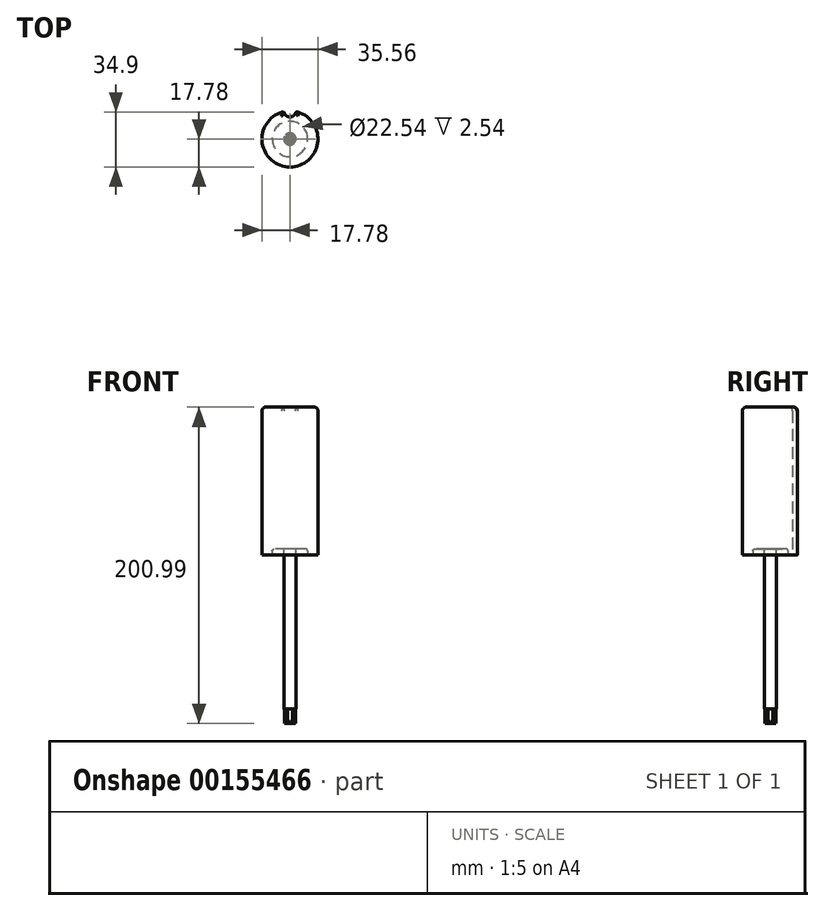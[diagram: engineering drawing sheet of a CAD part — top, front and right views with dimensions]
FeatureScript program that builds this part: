
annotation { "Feature Type Name" : "Feature", "Feature Type Description" : "" }
export const myFeature = defineFeature(function(context is Context, id is Id, definition is map)
    precondition{}
    {
        {
            var Q0;
            Q0=qCreatedBy(makeId("Top.planeOp"),FACE);
            var sketch = newSketch(context, id + "F0", { "sketchPlane" : qUnion([Q0])});
            skCircle(sketch, "E0", {"center": v(0, 0) * mm, "radius": 17.78 * mm});
            skSolve(sketch);
        }
        {
            var Q0;
            Q0=makeQuery(id+"F0.imprint","IMPRINT",FACE,{"disambiguationData":[TD([[makeQuery(id+"F0.imprint","IMPRINT",EDGE,{"derivedFrom":sQuery(id+"F0.wireOp",EDGE,"E0")}),1.0]])]});
            extrude(context, id + "F1", {"entities" : qUnion([Q0]), "depth" : 93.98 * mm});
        }
        {
            var Q0;
            Q0=qCreatedBy(makeId("Right.planeOp"),FACE);
            var sketch = newSketch(context, id + "F2", { "sketchPlane" : qUnion([Q0])});
            skLineSegment(sketch, "E1", {"start": v(0, 0) * mm, "end": v(0, -11.6) * mm});
            skLineSegment(sketch, "E2", {"start": v(0, -11.6) * mm, "end": v(8.75, -11.6) * mm});
            skLineSegment(sketch, "E3", {"start": v(8.75, -11.6) * mm, "end": v(6.7, 0) * mm});
            skLineSegment(sketch, "E4", {"start": v(6.7, 0) * mm, "end": v(0, 0) * mm});
            skSolve(sketch);
        }
        {
            var Q0;
            Q0=qCreatedBy(makeId("Top.planeOp"),FACE);
            var sketch = newSketch(context, id + "F3", { "sketchPlane" : qUnion([Q0])});
            skCircle(sketch, "E5", {"center": v(0, 17.78) * mm, "radius": 3.76 * mm});
            skSolve(sketch);
        }
        {
            var Q0;
            Q0=makeQuery(id+"F3.imprint","IMPRINT",FACE,{"disambiguationData":[TD([[makeQuery(id+"F3.imprint","IMPRINT",EDGE,{"derivedFrom":sQuery(id+"F3.wireOp",EDGE,"E5")}),1.0]])]});
            extrude(context, id + "F4", {"entities" : qUnion([Q0]), "operationType" : NewBodyOperationType.REMOVE, "depth" : 103.63 * mm});
        }
        {
            var Q0;
            Q0=makeQuery(id+"F4.boolean.opBoolean","INTERSECT",EDGE,{"disambiguationData":[OD(0.0)],"derivedFrom":[makeQuery(id+"F1.opExtrude","SWEPT_FACE",FACE,{"disambiguationData":[OSD([sQuery(id+"F0.wireOp",EDGE,"E0")])]}),makeQuery(id+"F4.opExtrude","SWEPT_FACE",FACE,{"disambiguationData":[OSD([sQuery(id+"F3.wireOp",EDGE,"E5")])]})]});
            var Q1;
            Q1=makeQuery(id+"F4.boolean.opBoolean","INTERSECT",EDGE,{"disambiguationData":[OD(1.0)],"derivedFrom":[makeQuery(id+"F1.opExtrude","SWEPT_FACE",FACE,{"disambiguationData":[OSD([sQuery(id+"F0.wireOp",EDGE,"E0")])]}),makeQuery(id+"F4.opExtrude","SWEPT_FACE",FACE,{"disambiguationData":[OSD([sQuery(id+"F3.wireOp",EDGE,"E5")])]})]});
            fillet(context, id + "F5", {"entities" : qUnion([Q0, Q1]), "radius" : 1.27 * mm, "tangentPropagation" : true, "allowEdgeOverflow" : false});
        }
        {
            var Q0;
            Q0=qCreatedBy(makeId("Top.planeOp"),FACE);
            var sketch = newSketch(context, id + "F6", { "sketchPlane" : qUnion([Q0])});
            skCircle(sketch, "E6", {"center": v(0, 0) * mm, "radius": 11.27 * mm});
            skSolve(sketch);
        }
        {
            var Q0;
            Q0=makeQuery(id+"F6.imprint","IMPRINT",FACE,{"disambiguationData":[TD([[makeQuery(id+"F6.imprint","IMPRINT",EDGE,{"derivedFrom":sQuery(id+"F6.wireOp",EDGE,"E6")}),1.0]])]});
            extrude(context, id + "F7", {"entities" : qUnion([Q0]), "operationType" : NewBodyOperationType.REMOVE, "depth" : 3.8 * mm});
        }
        {
            var Q0;
            Q0=makeQuery(id+"F7.boolean.opBoolean","COPY",EDGE,{"derivedFrom":makeQuery(id+"F7.opExtrude","CAP_EDGE",EDGE,{"disambiguationData":[OSD([sQuery(id+"F6.wireOp",EDGE,"E6")])],"isStart":true})});
            var Q1;
            Q1=makeQuery(id+"F7.boolean.opBoolean","COPY",EDGE,{"derivedFrom":makeQuery(id+"F7.opExtrude","CAP_EDGE",EDGE,{"disambiguationData":[OSD([sQuery(id+"F6.wireOp",EDGE,"E6")])],"isStart":false})});
            fillet(context, id + "F8", {"entities" : qUnion([Q0, Q1]), "radius" : 1.27 * mm, "tangentPropagation" : true, "allowEdgeOverflow" : false});
        }
        {
            var Q0;
            Q0=makeQuery(id+"F7.boolean.opBoolean","COPY",FACE,{"derivedFrom":makeQuery(id+"F7.opExtrude","CAP_FACE",FACE,{"disambiguationData":[OSD([sQuery(id+"F6.wireOp",EDGE,"E6")])],"isStart":false})});
            var sketch = newSketch(context, id + "F9", { "sketchPlane" : qUnion([Q0])});
            skCircle(sketch, "E7", {"center": v(0, 0) * mm, "radius": 3.81 * mm});
            skSolve(sketch);
        }
        {
            var Q0;
            Q0=makeQuery(id+"F9.imprint","IMPRINT",FACE,{"disambiguationData":[TD([[makeQuery(id+"F9.imprint","IMPRINT",EDGE,{"derivedFrom":sQuery(id+"F9.wireOp",EDGE,"E7")}),1.0]])]});
            extrude(context, id + "F10", {"entities" : qUnion([Q0]), "operationType" : NewBodyOperationType.ADD, "depth" : 101.6 * mm});
        }
        {
            var Q0;
            Q0=makeQuery(id+"FHcTJ38poMVbBsD_1.2.F4.boolean.opBoolean","INTERSECT",EDGE,{"derivedFrom":[makeQuery(id+"F1.opExtrude","CAP_FACE",FACE,{"disambiguationData":[OSD([sQuery(id+"F0.wireOp",EDGE,"E0")])],"isStart":false}),makeQuery(id+"FHcTJ38poMVbBsD_1.2.F4.opExtrude","SWEPT_FACE",FACE,{"disambiguationData":[OSD([sQuery(id+"F3.wireOp",EDGE,"E5")])]})]});
            var Q1;
            {var subQ0=sQuery(id+"F0.wireOp",EDGE,"E0");var subQ1=makeQuery(id+"F1.opExtrude","CAP_FACE",FACE,{"disambiguationData":[OSD([subQ0])],"isStart":false});var subQ2=sQuery(id+"F3.wireOp",EDGE,"E5");var subQ3=makeQuery(id+"F1.opExtrude","SWEPT_FACE",FACE,{"disambiguationData":[OSD([subQ0])]});Q1=makeQuery(id+"FHcTJ38poMVbBsD_1.2.F5.opFillet","BLEND_EDGE",EDGE,{"blendedFrom":[makeQuery(id+"FHcTJ38poMVbBsD_1.2.F4.boolean.opBoolean","INTERSECT",EDGE,{"disambiguationData":[OD(1.0)],"derivedFrom":[makeQuery(id+"FHcTJ38poMVbBsD_1.1.F4.boolean.opBoolean","SPLIT",FACE,{"disambiguationData":[TD([makeQuery(id+"F5.opFillet","BLEND_FACE",FACE,{"disambiguationData":[OSD([subQ0,subQ2]),TDD([makeQuery(id+"F4.boolean.opBoolean","INTERSECT",EDGE,{"disambiguationData":[OD(0.0)],"derivedFrom":[subQ3,makeQuery(id+"F4.opExtrude","SWEPT_FACE",FACE,{"disambiguationData":[OSD([subQ2])]})]})])]})])],"derivedFrom":subQ3}),makeQuery(id+"FHcTJ38poMVbBsD_1.2.F4.opExtrude","SWEPT_FACE",FACE,{"disambiguationData":[OSD([subQ2])]})]}),subQ1],"blendedInto":[subQ1]});}
            var Q2;
            {var subQ0=sQuery(id+"F0.wireOp",EDGE,"E0");var subQ1=makeQuery(id+"F1.opExtrude","SWEPT_FACE",FACE,{"disambiguationData":[OSD([subQ0])]});var subQ3=sQuery(id+"F3.wireOp",EDGE,"E5");var subQ4=makeQuery(id+"FHcTJ38poMVbBsD_1.1.F4.opExtrude","SWEPT_FACE",FACE,{"disambiguationData":[OSD([subQ3])]});Q2=makeQuery(id+"FHcTJ38poMVbBsD_1.2.F4.boolean.opBoolean","SPLIT",EDGE,{"disambiguationData":[TD([makeQuery(id+"FHcTJ38poMVbBsD_1.1.F5.opFillet","BLEND_FACE",FACE,{"disambiguationData":[OSD([subQ0,subQ3]),TDD([makeQuery(id+"FHcTJ38poMVbBsD_1.1.F4.boolean.opBoolean","INTERSECT",EDGE,{"disambiguationData":[OD(0.0)],"derivedFrom":[subQ1,subQ4]})])]})])],"derivedFrom":makeQuery(id+"FHcTJ38poMVbBsD_1.1.F4.boolean.opBoolean","SPLIT",EDGE,{"disambiguationData":[TD([makeQuery(id+"F5.opFillet","BLEND_FACE",FACE,{"disambiguationData":[OSD([subQ0,subQ3]),TDD([makeQuery(id+"F4.boolean.opBoolean","INTERSECT",EDGE,{"disambiguationData":[OD(0.0)],"derivedFrom":[subQ1,makeQuery(id+"F4.opExtrude","SWEPT_FACE",FACE,{"disambiguationData":[OSD([subQ3])]})]})])]})])],"derivedFrom":makeQuery(id+"F1.opExtrude","CAP_EDGE",EDGE,{"disambiguationData":[OSD([subQ0])],"isStart":false})})});}
            var Q3;
            Q3=makeQuery(id+"FHcTJ38poMVbBsD_1.1.F4.boolean.opBoolean","INTERSECT",EDGE,{"derivedFrom":[makeQuery(id+"F1.opExtrude","CAP_FACE",FACE,{"disambiguationData":[OSD([sQuery(id+"F0.wireOp",EDGE,"E0")])],"isStart":false}),makeQuery(id+"FHcTJ38poMVbBsD_1.1.F4.opExtrude","SWEPT_FACE",FACE,{"disambiguationData":[OSD([sQuery(id+"F3.wireOp",EDGE,"E5")])]})]});
            var Q4;
            {var subQ0=sQuery(id+"F0.wireOp",EDGE,"E0");Q4=makeQuery(id+"FHcTJ38poMVbBsD_1.1.F5.opFillet","BLEND_EDGE",EDGE,{"blendedFrom":[makeQuery(id+"FHcTJ38poMVbBsD_1.1.F4.boolean.opBoolean","INTERSECT",EDGE,{"disambiguationData":[OD(0.0)],"derivedFrom":[makeQuery(id+"F1.opExtrude","SWEPT_FACE",FACE,{"disambiguationData":[OSD([subQ0])]}),makeQuery(id+"FHcTJ38poMVbBsD_1.1.F4.opExtrude","SWEPT_FACE",FACE,{"disambiguationData":[OSD([sQuery(id+"F3.wireOp",EDGE,"E5")])]})]}),makeQuery(id+"F1.opExtrude","CAP_FACE",FACE,{"disambiguationData":[OSD([subQ0])],"isStart":false})],"blendedInto":[makeQuery(id+"F1.opExtrude","CAP_FACE",FACE,{"disambiguationData":[OSD([subQ0])],"isStart":false})]});}
            var Q5;
            {var subQ0=sQuery(id+"F0.wireOp",EDGE,"E0");Q5=makeQuery(id+"FHcTJ38poMVbBsD_1.1.F5.opFillet","BLEND_EDGE",EDGE,{"blendedFrom":[makeQuery(id+"FHcTJ38poMVbBsD_1.1.F4.boolean.opBoolean","INTERSECT",EDGE,{"disambiguationData":[OD(1.0)],"derivedFrom":[makeQuery(id+"F1.opExtrude","SWEPT_FACE",FACE,{"disambiguationData":[OSD([subQ0])]}),makeQuery(id+"FHcTJ38poMVbBsD_1.1.F4.opExtrude","SWEPT_FACE",FACE,{"disambiguationData":[OSD([sQuery(id+"F3.wireOp",EDGE,"E5")])]})]}),makeQuery(id+"F1.opExtrude","CAP_FACE",FACE,{"disambiguationData":[OSD([subQ0])],"isStart":false})],"blendedInto":[makeQuery(id+"F1.opExtrude","CAP_FACE",FACE,{"disambiguationData":[OSD([subQ0])],"isStart":false})]});}
            var Q6;
            {var subQ0=sQuery(id+"F0.wireOp",EDGE,"E0");var subQ1=makeQuery(id+"F1.opExtrude","SWEPT_FACE",FACE,{"disambiguationData":[OSD([subQ0])]});var subQ2=sQuery(id+"F3.wireOp",EDGE,"E5");Q6=makeQuery(id+"FHcTJ38poMVbBsD_1.1.F4.boolean.opBoolean","SPLIT",EDGE,{"disambiguationData":[TD([makeQuery(id+"F5.opFillet","BLEND_FACE",FACE,{"disambiguationData":[OSD([subQ0,subQ2]),TDD([makeQuery(id+"F4.boolean.opBoolean","INTERSECT",EDGE,{"disambiguationData":[OD(1.0)],"derivedFrom":[subQ1,makeQuery(id+"F4.opExtrude","SWEPT_FACE",FACE,{"disambiguationData":[OSD([subQ2])]})]})])]})])],"derivedFrom":makeQuery(id+"F1.opExtrude","CAP_EDGE",EDGE,{"disambiguationData":[OSD([subQ0])],"isStart":false})});}
            var Q7;
            {var subQ0=sQuery(id+"F0.wireOp",EDGE,"E0");Q7=makeQuery(id+"F5.opFillet","BLEND_EDGE",EDGE,{"blendedFrom":[makeQuery(id+"F4.boolean.opBoolean","INTERSECT",EDGE,{"disambiguationData":[OD(1.0)],"derivedFrom":[makeQuery(id+"F1.opExtrude","SWEPT_FACE",FACE,{"disambiguationData":[OSD([subQ0])]}),makeQuery(id+"F4.opExtrude","SWEPT_FACE",FACE,{"disambiguationData":[OSD([sQuery(id+"F3.wireOp",EDGE,"E5")])]})]}),makeQuery(id+"F1.opExtrude","CAP_FACE",FACE,{"disambiguationData":[OSD([subQ0])],"isStart":false})],"blendedInto":[makeQuery(id+"F1.opExtrude","CAP_FACE",FACE,{"disambiguationData":[OSD([subQ0])],"isStart":false})]});}
            var Q8;
            Q8=makeQuery(id+"F4.boolean.opBoolean","INTERSECT",EDGE,{"derivedFrom":[makeQuery(id+"F1.opExtrude","CAP_FACE",FACE,{"disambiguationData":[OSD([sQuery(id+"F0.wireOp",EDGE,"E0")])],"isStart":false}),makeQuery(id+"F4.opExtrude","SWEPT_FACE",FACE,{"disambiguationData":[OSD([sQuery(id+"F3.wireOp",EDGE,"E5")])]})]});
            var Q9;
            {var subQ0=sQuery(id+"F0.wireOp",EDGE,"E0");Q9=makeQuery(id+"F5.opFillet","BLEND_EDGE",EDGE,{"blendedFrom":[makeQuery(id+"F4.boolean.opBoolean","INTERSECT",EDGE,{"disambiguationData":[OD(0.0)],"derivedFrom":[makeQuery(id+"F1.opExtrude","SWEPT_FACE",FACE,{"disambiguationData":[OSD([subQ0])]}),makeQuery(id+"F4.opExtrude","SWEPT_FACE",FACE,{"disambiguationData":[OSD([sQuery(id+"F3.wireOp",EDGE,"E5")])]})]}),makeQuery(id+"F1.opExtrude","CAP_FACE",FACE,{"disambiguationData":[OSD([subQ0])],"isStart":false})],"blendedInto":[makeQuery(id+"F1.opExtrude","CAP_FACE",FACE,{"disambiguationData":[OSD([subQ0])],"isStart":false})]});}
            var Q10;
            {var subQ0=sQuery(id+"F0.wireOp",EDGE,"E0");var subQ1=makeQuery(id+"F1.opExtrude","SWEPT_FACE",FACE,{"disambiguationData":[OSD([subQ0])]});var subQ3=sQuery(id+"F3.wireOp",EDGE,"E5");var subQ4=makeQuery(id+"F5.opFillet","BLEND_FACE",FACE,{"disambiguationData":[OSD([subQ0,subQ3]),TDD([makeQuery(id+"F4.boolean.opBoolean","INTERSECT",EDGE,{"disambiguationData":[OD(0.0)],"derivedFrom":[subQ1,makeQuery(id+"F4.opExtrude","SWEPT_FACE",FACE,{"disambiguationData":[OSD([subQ3])]})]})])]});Q10=makeQuery(id+"FHcTJ38poMVbBsD_1.7.F4.boolean.opBoolean","SPLIT",EDGE,{"disambiguationData":[TD([subQ4])],"derivedFrom":makeQuery(id+"FHcTJ38poMVbBsD_1.6.F4.boolean.opBoolean","SPLIT",EDGE,{"disambiguationData":[TD([subQ4])],"derivedFrom":makeQuery(id+"FHcTJ38poMVbBsD_1.5.F4.boolean.opBoolean","SPLIT",EDGE,{"disambiguationData":[TD([subQ4])],"derivedFrom":makeQuery(id+"FHcTJ38poMVbBsD_1.4.F4.boolean.opBoolean","SPLIT",EDGE,{"disambiguationData":[TD([subQ4])],"derivedFrom":makeQuery(id+"FHcTJ38poMVbBsD_1.3.F4.boolean.opBoolean","SPLIT",EDGE,{"disambiguationData":[TD([subQ4])],"derivedFrom":makeQuery(id+"FHcTJ38poMVbBsD_1.2.F4.boolean.opBoolean","SPLIT",EDGE,{"disambiguationData":[TD([subQ4])],"derivedFrom":makeQuery(id+"FHcTJ38poMVbBsD_1.1.F4.boolean.opBoolean","SPLIT",EDGE,{"disambiguationData":[TD([subQ4])],"derivedFrom":makeQuery(id+"F1.opExtrude","CAP_EDGE",EDGE,{"disambiguationData":[OSD([subQ0])],"isStart":false})})})})})})})});}
            var Q11;
            {var subQ0=sQuery(id+"F0.wireOp",EDGE,"E0");var subQ1=makeQuery(id+"F1.opExtrude","CAP_FACE",FACE,{"disambiguationData":[OSD([subQ0])],"isStart":false});var subQ2=sQuery(id+"F3.wireOp",EDGE,"E5");var subQ4=makeQuery(id+"F1.opExtrude","SWEPT_FACE",FACE,{"disambiguationData":[OSD([subQ0])]});var subQ5=makeQuery(id+"F5.opFillet","BLEND_FACE",FACE,{"disambiguationData":[OSD([subQ0,subQ2]),TDD([makeQuery(id+"F4.boolean.opBoolean","INTERSECT",EDGE,{"disambiguationData":[OD(0.0)],"derivedFrom":[subQ4,makeQuery(id+"F4.opExtrude","SWEPT_FACE",FACE,{"disambiguationData":[OSD([subQ2])]})]})])]});Q11=makeQuery(id+"FHcTJ38poMVbBsD_1.7.F5.opFillet","BLEND_EDGE",EDGE,{"blendedFrom":[makeQuery(id+"FHcTJ38poMVbBsD_1.7.F4.boolean.opBoolean","INTERSECT",EDGE,{"disambiguationData":[OD(0.0)],"derivedFrom":[makeQuery(id+"FHcTJ38poMVbBsD_1.6.F4.boolean.opBoolean","SPLIT",FACE,{"disambiguationData":[TD([subQ5])],"derivedFrom":makeQuery(id+"FHcTJ38poMVbBsD_1.5.F4.boolean.opBoolean","SPLIT",FACE,{"disambiguationData":[TD([subQ5])],"derivedFrom":makeQuery(id+"FHcTJ38poMVbBsD_1.4.F4.boolean.opBoolean","SPLIT",FACE,{"disambiguationData":[TD([subQ5])],"derivedFrom":makeQuery(id+"FHcTJ38poMVbBsD_1.3.F4.boolean.opBoolean","SPLIT",FACE,{"disambiguationData":[TD([subQ5])],"derivedFrom":makeQuery(id+"FHcTJ38poMVbBsD_1.2.F4.boolean.opBoolean","SPLIT",FACE,{"disambiguationData":[TD([subQ5])],"derivedFrom":makeQuery(id+"FHcTJ38poMVbBsD_1.1.F4.boolean.opBoolean","SPLIT",FACE,{"disambiguationData":[TD([subQ5])],"derivedFrom":subQ4})})})})})}),makeQuery(id+"FHcTJ38poMVbBsD_1.7.F4.opExtrude","SWEPT_FACE",FACE,{"disambiguationData":[OSD([subQ2])]})]}),subQ1],"blendedInto":[subQ1]});}
            var Q12;
            Q12=makeQuery(id+"FHcTJ38poMVbBsD_1.7.F4.boolean.opBoolean","INTERSECT",EDGE,{"derivedFrom":[makeQuery(id+"F1.opExtrude","CAP_FACE",FACE,{"disambiguationData":[OSD([sQuery(id+"F0.wireOp",EDGE,"E0")])],"isStart":false}),makeQuery(id+"FHcTJ38poMVbBsD_1.7.F4.opExtrude","SWEPT_FACE",FACE,{"disambiguationData":[OSD([sQuery(id+"F3.wireOp",EDGE,"E5")])]})]});
            var Q13;
            {var subQ0=sQuery(id+"F0.wireOp",EDGE,"E0");var subQ1=makeQuery(id+"F1.opExtrude","CAP_FACE",FACE,{"disambiguationData":[OSD([subQ0])],"isStart":false});var subQ2=sQuery(id+"F3.wireOp",EDGE,"E5");var subQ4=makeQuery(id+"F1.opExtrude","SWEPT_FACE",FACE,{"disambiguationData":[OSD([subQ0])]});var subQ5=makeQuery(id+"F5.opFillet","BLEND_FACE",FACE,{"disambiguationData":[OSD([subQ0,subQ2]),TDD([makeQuery(id+"F4.boolean.opBoolean","INTERSECT",EDGE,{"disambiguationData":[OD(0.0)],"derivedFrom":[subQ4,makeQuery(id+"F4.opExtrude","SWEPT_FACE",FACE,{"disambiguationData":[OSD([subQ2])]})]})])]});Q13=makeQuery(id+"FHcTJ38poMVbBsD_1.7.F5.opFillet","BLEND_EDGE",EDGE,{"blendedFrom":[makeQuery(id+"FHcTJ38poMVbBsD_1.7.F4.boolean.opBoolean","INTERSECT",EDGE,{"disambiguationData":[OD(1.0)],"derivedFrom":[makeQuery(id+"FHcTJ38poMVbBsD_1.6.F4.boolean.opBoolean","SPLIT",FACE,{"disambiguationData":[TD([subQ5])],"derivedFrom":makeQuery(id+"FHcTJ38poMVbBsD_1.5.F4.boolean.opBoolean","SPLIT",FACE,{"disambiguationData":[TD([subQ5])],"derivedFrom":makeQuery(id+"FHcTJ38poMVbBsD_1.4.F4.boolean.opBoolean","SPLIT",FACE,{"disambiguationData":[TD([subQ5])],"derivedFrom":makeQuery(id+"FHcTJ38poMVbBsD_1.3.F4.boolean.opBoolean","SPLIT",FACE,{"disambiguationData":[TD([subQ5])],"derivedFrom":makeQuery(id+"FHcTJ38poMVbBsD_1.2.F4.boolean.opBoolean","SPLIT",FACE,{"disambiguationData":[TD([subQ5])],"derivedFrom":makeQuery(id+"FHcTJ38poMVbBsD_1.1.F4.boolean.opBoolean","SPLIT",FACE,{"disambiguationData":[TD([subQ5])],"derivedFrom":subQ4})})})})})}),makeQuery(id+"FHcTJ38poMVbBsD_1.7.F4.opExtrude","SWEPT_FACE",FACE,{"disambiguationData":[OSD([subQ2])]})]}),subQ1],"blendedInto":[subQ1]});}
            var Q14;
            {var subQ0=sQuery(id+"F0.wireOp",EDGE,"E0");var subQ1=makeQuery(id+"F1.opExtrude","SWEPT_FACE",FACE,{"disambiguationData":[OSD([subQ0])]});var subQ2=sQuery(id+"F3.wireOp",EDGE,"E5");var subQ3=makeQuery(id+"FHcTJ38poMVbBsD_1.6.F4.opExtrude","SWEPT_FACE",FACE,{"disambiguationData":[OSD([subQ2])]});var subQ7=makeQuery(id+"F5.opFillet","BLEND_FACE",FACE,{"disambiguationData":[OSD([subQ0,subQ2]),TDD([makeQuery(id+"F4.boolean.opBoolean","INTERSECT",EDGE,{"disambiguationData":[OD(0.0)],"derivedFrom":[subQ1,makeQuery(id+"F4.opExtrude","SWEPT_FACE",FACE,{"disambiguationData":[OSD([subQ2])]})]})])]});Q14=makeQuery(id+"FHcTJ38poMVbBsD_1.7.F4.boolean.opBoolean","SPLIT",EDGE,{"disambiguationData":[TD([makeQuery(id+"FHcTJ38poMVbBsD_1.6.F5.opFillet","BLEND_FACE",FACE,{"disambiguationData":[OSD([subQ0,subQ2]),TDD([makeQuery(id+"FHcTJ38poMVbBsD_1.6.F4.boolean.opBoolean","INTERSECT",EDGE,{"disambiguationData":[OD(0.0)],"derivedFrom":[makeQuery(id+"FHcTJ38poMVbBsD_1.5.F4.boolean.opBoolean","SPLIT",FACE,{"disambiguationData":[TD([subQ7])],"derivedFrom":makeQuery(id+"FHcTJ38poMVbBsD_1.4.F4.boolean.opBoolean","SPLIT",FACE,{"disambiguationData":[TD([subQ7])],"derivedFrom":makeQuery(id+"FHcTJ38poMVbBsD_1.3.F4.boolean.opBoolean","SPLIT",FACE,{"disambiguationData":[TD([subQ7])],"derivedFrom":makeQuery(id+"FHcTJ38poMVbBsD_1.2.F4.boolean.opBoolean","SPLIT",FACE,{"disambiguationData":[TD([subQ7])],"derivedFrom":makeQuery(id+"FHcTJ38poMVbBsD_1.1.F4.boolean.opBoolean","SPLIT",FACE,{"disambiguationData":[TD([subQ7])],"derivedFrom":subQ1})})})})}),subQ3]})])]})])],"derivedFrom":makeQuery(id+"FHcTJ38poMVbBsD_1.6.F4.boolean.opBoolean","SPLIT",EDGE,{"disambiguationData":[TD([subQ7])],"derivedFrom":makeQuery(id+"FHcTJ38poMVbBsD_1.5.F4.boolean.opBoolean","SPLIT",EDGE,{"disambiguationData":[TD([subQ7])],"derivedFrom":makeQuery(id+"FHcTJ38poMVbBsD_1.4.F4.boolean.opBoolean","SPLIT",EDGE,{"disambiguationData":[TD([subQ7])],"derivedFrom":makeQuery(id+"FHcTJ38poMVbBsD_1.3.F4.boolean.opBoolean","SPLIT",EDGE,{"disambiguationData":[TD([subQ7])],"derivedFrom":makeQuery(id+"FHcTJ38poMVbBsD_1.2.F4.boolean.opBoolean","SPLIT",EDGE,{"disambiguationData":[TD([subQ7])],"derivedFrom":makeQuery(id+"FHcTJ38poMVbBsD_1.1.F4.boolean.opBoolean","SPLIT",EDGE,{"disambiguationData":[TD([subQ7])],"derivedFrom":makeQuery(id+"F1.opExtrude","CAP_EDGE",EDGE,{"disambiguationData":[OSD([subQ0])],"isStart":false})})})})})})})});}
            var Q15;
            {var subQ0=sQuery(id+"F0.wireOp",EDGE,"E0");var subQ1=makeQuery(id+"F1.opExtrude","CAP_FACE",FACE,{"disambiguationData":[OSD([subQ0])],"isStart":false});var subQ2=sQuery(id+"F3.wireOp",EDGE,"E5");var subQ4=makeQuery(id+"F1.opExtrude","SWEPT_FACE",FACE,{"disambiguationData":[OSD([subQ0])]});var subQ5=makeQuery(id+"F5.opFillet","BLEND_FACE",FACE,{"disambiguationData":[OSD([subQ0,subQ2]),TDD([makeQuery(id+"F4.boolean.opBoolean","INTERSECT",EDGE,{"disambiguationData":[OD(0.0)],"derivedFrom":[subQ4,makeQuery(id+"F4.opExtrude","SWEPT_FACE",FACE,{"disambiguationData":[OSD([subQ2])]})]})])]});Q15=makeQuery(id+"FHcTJ38poMVbBsD_1.6.F5.opFillet","BLEND_EDGE",EDGE,{"blendedFrom":[makeQuery(id+"FHcTJ38poMVbBsD_1.6.F4.boolean.opBoolean","INTERSECT",EDGE,{"disambiguationData":[OD(0.0)],"derivedFrom":[makeQuery(id+"FHcTJ38poMVbBsD_1.5.F4.boolean.opBoolean","SPLIT",FACE,{"disambiguationData":[TD([subQ5])],"derivedFrom":makeQuery(id+"FHcTJ38poMVbBsD_1.4.F4.boolean.opBoolean","SPLIT",FACE,{"disambiguationData":[TD([subQ5])],"derivedFrom":makeQuery(id+"FHcTJ38poMVbBsD_1.3.F4.boolean.opBoolean","SPLIT",FACE,{"disambiguationData":[TD([subQ5])],"derivedFrom":makeQuery(id+"FHcTJ38poMVbBsD_1.2.F4.boolean.opBoolean","SPLIT",FACE,{"disambiguationData":[TD([subQ5])],"derivedFrom":makeQuery(id+"FHcTJ38poMVbBsD_1.1.F4.boolean.opBoolean","SPLIT",FACE,{"disambiguationData":[TD([subQ5])],"derivedFrom":subQ4})})})})}),makeQuery(id+"FHcTJ38poMVbBsD_1.6.F4.opExtrude","SWEPT_FACE",FACE,{"disambiguationData":[OSD([subQ2])]})]}),subQ1],"blendedInto":[subQ1]});}
            var Q16;
            Q16=makeQuery(id+"FHcTJ38poMVbBsD_1.6.F4.boolean.opBoolean","INTERSECT",EDGE,{"derivedFrom":[makeQuery(id+"F1.opExtrude","CAP_FACE",FACE,{"disambiguationData":[OSD([sQuery(id+"F0.wireOp",EDGE,"E0")])],"isStart":false}),makeQuery(id+"FHcTJ38poMVbBsD_1.6.F4.opExtrude","SWEPT_FACE",FACE,{"disambiguationData":[OSD([sQuery(id+"F3.wireOp",EDGE,"E5")])]})]});
            var Q17;
            {var subQ0=sQuery(id+"F0.wireOp",EDGE,"E0");var subQ1=makeQuery(id+"F1.opExtrude","CAP_FACE",FACE,{"disambiguationData":[OSD([subQ0])],"isStart":false});var subQ2=sQuery(id+"F3.wireOp",EDGE,"E5");var subQ4=makeQuery(id+"F1.opExtrude","SWEPT_FACE",FACE,{"disambiguationData":[OSD([subQ0])]});var subQ5=makeQuery(id+"F5.opFillet","BLEND_FACE",FACE,{"disambiguationData":[OSD([subQ0,subQ2]),TDD([makeQuery(id+"F4.boolean.opBoolean","INTERSECT",EDGE,{"disambiguationData":[OD(0.0)],"derivedFrom":[subQ4,makeQuery(id+"F4.opExtrude","SWEPT_FACE",FACE,{"disambiguationData":[OSD([subQ2])]})]})])]});Q17=makeQuery(id+"FHcTJ38poMVbBsD_1.6.F5.opFillet","BLEND_EDGE",EDGE,{"blendedFrom":[makeQuery(id+"FHcTJ38poMVbBsD_1.6.F4.boolean.opBoolean","INTERSECT",EDGE,{"disambiguationData":[OD(1.0)],"derivedFrom":[makeQuery(id+"FHcTJ38poMVbBsD_1.5.F4.boolean.opBoolean","SPLIT",FACE,{"disambiguationData":[TD([subQ5])],"derivedFrom":makeQuery(id+"FHcTJ38poMVbBsD_1.4.F4.boolean.opBoolean","SPLIT",FACE,{"disambiguationData":[TD([subQ5])],"derivedFrom":makeQuery(id+"FHcTJ38poMVbBsD_1.3.F4.boolean.opBoolean","SPLIT",FACE,{"disambiguationData":[TD([subQ5])],"derivedFrom":makeQuery(id+"FHcTJ38poMVbBsD_1.2.F4.boolean.opBoolean","SPLIT",FACE,{"disambiguationData":[TD([subQ5])],"derivedFrom":makeQuery(id+"FHcTJ38poMVbBsD_1.1.F4.boolean.opBoolean","SPLIT",FACE,{"disambiguationData":[TD([subQ5])],"derivedFrom":subQ4})})})})}),makeQuery(id+"FHcTJ38poMVbBsD_1.6.F4.opExtrude","SWEPT_FACE",FACE,{"disambiguationData":[OSD([subQ2])]})]}),subQ1],"blendedInto":[subQ1]});}
            var Q18;
            {var subQ0=sQuery(id+"F0.wireOp",EDGE,"E0");var subQ1=makeQuery(id+"F1.opExtrude","SWEPT_FACE",FACE,{"disambiguationData":[OSD([subQ0])]});var subQ2=sQuery(id+"F3.wireOp",EDGE,"E5");var subQ4=makeQuery(id+"FHcTJ38poMVbBsD_1.5.F4.opExtrude","SWEPT_FACE",FACE,{"disambiguationData":[OSD([subQ2])]});var subQ7=makeQuery(id+"F5.opFillet","BLEND_FACE",FACE,{"disambiguationData":[OSD([subQ0,subQ2]),TDD([makeQuery(id+"F4.boolean.opBoolean","INTERSECT",EDGE,{"disambiguationData":[OD(0.0)],"derivedFrom":[subQ1,makeQuery(id+"F4.opExtrude","SWEPT_FACE",FACE,{"disambiguationData":[OSD([subQ2])]})]})])]});Q18=makeQuery(id+"FHcTJ38poMVbBsD_1.6.F4.boolean.opBoolean","SPLIT",EDGE,{"disambiguationData":[TD([makeQuery(id+"FHcTJ38poMVbBsD_1.5.F5.opFillet","BLEND_FACE",FACE,{"disambiguationData":[OSD([subQ0,subQ2]),TDD([makeQuery(id+"FHcTJ38poMVbBsD_1.5.F4.boolean.opBoolean","INTERSECT",EDGE,{"disambiguationData":[OD(0.0)],"derivedFrom":[makeQuery(id+"FHcTJ38poMVbBsD_1.4.F4.boolean.opBoolean","SPLIT",FACE,{"disambiguationData":[TD([subQ7])],"derivedFrom":makeQuery(id+"FHcTJ38poMVbBsD_1.3.F4.boolean.opBoolean","SPLIT",FACE,{"disambiguationData":[TD([subQ7])],"derivedFrom":makeQuery(id+"FHcTJ38poMVbBsD_1.2.F4.boolean.opBoolean","SPLIT",FACE,{"disambiguationData":[TD([subQ7])],"derivedFrom":makeQuery(id+"FHcTJ38poMVbBsD_1.1.F4.boolean.opBoolean","SPLIT",FACE,{"disambiguationData":[TD([subQ7])],"derivedFrom":subQ1})})})}),subQ4]})])]})])],"derivedFrom":makeQuery(id+"FHcTJ38poMVbBsD_1.5.F4.boolean.opBoolean","SPLIT",EDGE,{"disambiguationData":[TD([subQ7])],"derivedFrom":makeQuery(id+"FHcTJ38poMVbBsD_1.4.F4.boolean.opBoolean","SPLIT",EDGE,{"disambiguationData":[TD([subQ7])],"derivedFrom":makeQuery(id+"FHcTJ38poMVbBsD_1.3.F4.boolean.opBoolean","SPLIT",EDGE,{"disambiguationData":[TD([subQ7])],"derivedFrom":makeQuery(id+"FHcTJ38poMVbBsD_1.2.F4.boolean.opBoolean","SPLIT",EDGE,{"disambiguationData":[TD([subQ7])],"derivedFrom":makeQuery(id+"FHcTJ38poMVbBsD_1.1.F4.boolean.opBoolean","SPLIT",EDGE,{"disambiguationData":[TD([subQ7])],"derivedFrom":makeQuery(id+"F1.opExtrude","CAP_EDGE",EDGE,{"disambiguationData":[OSD([subQ0])],"isStart":false})})})})})})});}
            var Q19;
            {var subQ0=sQuery(id+"F0.wireOp",EDGE,"E0");var subQ1=makeQuery(id+"F1.opExtrude","CAP_FACE",FACE,{"disambiguationData":[OSD([subQ0])],"isStart":false});var subQ2=sQuery(id+"F3.wireOp",EDGE,"E5");var subQ4=makeQuery(id+"F1.opExtrude","SWEPT_FACE",FACE,{"disambiguationData":[OSD([subQ0])]});var subQ5=makeQuery(id+"F5.opFillet","BLEND_FACE",FACE,{"disambiguationData":[OSD([subQ0,subQ2]),TDD([makeQuery(id+"F4.boolean.opBoolean","INTERSECT",EDGE,{"disambiguationData":[OD(0.0)],"derivedFrom":[subQ4,makeQuery(id+"F4.opExtrude","SWEPT_FACE",FACE,{"disambiguationData":[OSD([subQ2])]})]})])]});Q19=makeQuery(id+"FHcTJ38poMVbBsD_1.5.F5.opFillet","BLEND_EDGE",EDGE,{"blendedFrom":[makeQuery(id+"FHcTJ38poMVbBsD_1.5.F4.boolean.opBoolean","INTERSECT",EDGE,{"disambiguationData":[OD(0.0)],"derivedFrom":[makeQuery(id+"FHcTJ38poMVbBsD_1.4.F4.boolean.opBoolean","SPLIT",FACE,{"disambiguationData":[TD([subQ5])],"derivedFrom":makeQuery(id+"FHcTJ38poMVbBsD_1.3.F4.boolean.opBoolean","SPLIT",FACE,{"disambiguationData":[TD([subQ5])],"derivedFrom":makeQuery(id+"FHcTJ38poMVbBsD_1.2.F4.boolean.opBoolean","SPLIT",FACE,{"disambiguationData":[TD([subQ5])],"derivedFrom":makeQuery(id+"FHcTJ38poMVbBsD_1.1.F4.boolean.opBoolean","SPLIT",FACE,{"disambiguationData":[TD([subQ5])],"derivedFrom":subQ4})})})}),makeQuery(id+"FHcTJ38poMVbBsD_1.5.F4.opExtrude","SWEPT_FACE",FACE,{"disambiguationData":[OSD([subQ2])]})]}),subQ1],"blendedInto":[subQ1]});}
            var Q20;
            Q20=makeQuery(id+"FHcTJ38poMVbBsD_1.5.F4.boolean.opBoolean","INTERSECT",EDGE,{"derivedFrom":[makeQuery(id+"F1.opExtrude","CAP_FACE",FACE,{"disambiguationData":[OSD([sQuery(id+"F0.wireOp",EDGE,"E0")])],"isStart":false}),makeQuery(id+"FHcTJ38poMVbBsD_1.5.F4.opExtrude","SWEPT_FACE",FACE,{"disambiguationData":[OSD([sQuery(id+"F3.wireOp",EDGE,"E5")])]})]});
            var Q21;
            {var subQ0=sQuery(id+"F0.wireOp",EDGE,"E0");var subQ1=makeQuery(id+"F1.opExtrude","CAP_FACE",FACE,{"disambiguationData":[OSD([subQ0])],"isStart":false});var subQ2=sQuery(id+"F3.wireOp",EDGE,"E5");var subQ4=makeQuery(id+"F1.opExtrude","SWEPT_FACE",FACE,{"disambiguationData":[OSD([subQ0])]});var subQ5=makeQuery(id+"F5.opFillet","BLEND_FACE",FACE,{"disambiguationData":[OSD([subQ0,subQ2]),TDD([makeQuery(id+"F4.boolean.opBoolean","INTERSECT",EDGE,{"disambiguationData":[OD(0.0)],"derivedFrom":[subQ4,makeQuery(id+"F4.opExtrude","SWEPT_FACE",FACE,{"disambiguationData":[OSD([subQ2])]})]})])]});Q21=makeQuery(id+"FHcTJ38poMVbBsD_1.5.F5.opFillet","BLEND_EDGE",EDGE,{"blendedFrom":[makeQuery(id+"FHcTJ38poMVbBsD_1.5.F4.boolean.opBoolean","INTERSECT",EDGE,{"disambiguationData":[OD(1.0)],"derivedFrom":[makeQuery(id+"FHcTJ38poMVbBsD_1.4.F4.boolean.opBoolean","SPLIT",FACE,{"disambiguationData":[TD([subQ5])],"derivedFrom":makeQuery(id+"FHcTJ38poMVbBsD_1.3.F4.boolean.opBoolean","SPLIT",FACE,{"disambiguationData":[TD([subQ5])],"derivedFrom":makeQuery(id+"FHcTJ38poMVbBsD_1.2.F4.boolean.opBoolean","SPLIT",FACE,{"disambiguationData":[TD([subQ5])],"derivedFrom":makeQuery(id+"FHcTJ38poMVbBsD_1.1.F4.boolean.opBoolean","SPLIT",FACE,{"disambiguationData":[TD([subQ5])],"derivedFrom":subQ4})})})}),makeQuery(id+"FHcTJ38poMVbBsD_1.5.F4.opExtrude","SWEPT_FACE",FACE,{"disambiguationData":[OSD([subQ2])]})]}),subQ1],"blendedInto":[subQ1]});}
            var Q22;
            {var subQ0=sQuery(id+"F0.wireOp",EDGE,"E0");var subQ1=makeQuery(id+"F1.opExtrude","SWEPT_FACE",FACE,{"disambiguationData":[OSD([subQ0])]});var subQ2=sQuery(id+"F3.wireOp",EDGE,"E5");var subQ4=makeQuery(id+"FHcTJ38poMVbBsD_1.4.F4.opExtrude","SWEPT_FACE",FACE,{"disambiguationData":[OSD([subQ2])]});var subQ6=makeQuery(id+"F5.opFillet","BLEND_FACE",FACE,{"disambiguationData":[OSD([subQ0,subQ2]),TDD([makeQuery(id+"F4.boolean.opBoolean","INTERSECT",EDGE,{"disambiguationData":[OD(0.0)],"derivedFrom":[subQ1,makeQuery(id+"F4.opExtrude","SWEPT_FACE",FACE,{"disambiguationData":[OSD([subQ2])]})]})])]});Q22=makeQuery(id+"FHcTJ38poMVbBsD_1.5.F4.boolean.opBoolean","SPLIT",EDGE,{"disambiguationData":[TD([makeQuery(id+"FHcTJ38poMVbBsD_1.4.F5.opFillet","BLEND_FACE",FACE,{"disambiguationData":[OSD([subQ0,subQ2]),TDD([makeQuery(id+"FHcTJ38poMVbBsD_1.4.F4.boolean.opBoolean","INTERSECT",EDGE,{"disambiguationData":[OD(0.0)],"derivedFrom":[makeQuery(id+"FHcTJ38poMVbBsD_1.3.F4.boolean.opBoolean","SPLIT",FACE,{"disambiguationData":[TD([subQ6])],"derivedFrom":makeQuery(id+"FHcTJ38poMVbBsD_1.2.F4.boolean.opBoolean","SPLIT",FACE,{"disambiguationData":[TD([subQ6])],"derivedFrom":makeQuery(id+"FHcTJ38poMVbBsD_1.1.F4.boolean.opBoolean","SPLIT",FACE,{"disambiguationData":[TD([subQ6])],"derivedFrom":subQ1})})}),subQ4]})])]})])],"derivedFrom":makeQuery(id+"FHcTJ38poMVbBsD_1.4.F4.boolean.opBoolean","SPLIT",EDGE,{"disambiguationData":[TD([subQ6])],"derivedFrom":makeQuery(id+"FHcTJ38poMVbBsD_1.3.F4.boolean.opBoolean","SPLIT",EDGE,{"disambiguationData":[TD([subQ6])],"derivedFrom":makeQuery(id+"FHcTJ38poMVbBsD_1.2.F4.boolean.opBoolean","SPLIT",EDGE,{"disambiguationData":[TD([subQ6])],"derivedFrom":makeQuery(id+"FHcTJ38poMVbBsD_1.1.F4.boolean.opBoolean","SPLIT",EDGE,{"disambiguationData":[TD([subQ6])],"derivedFrom":makeQuery(id+"F1.opExtrude","CAP_EDGE",EDGE,{"disambiguationData":[OSD([subQ0])],"isStart":false})})})})})});}
            var Q23;
            {var subQ0=sQuery(id+"F0.wireOp",EDGE,"E0");var subQ1=makeQuery(id+"F1.opExtrude","CAP_FACE",FACE,{"disambiguationData":[OSD([subQ0])],"isStart":false});var subQ2=sQuery(id+"F3.wireOp",EDGE,"E5");var subQ4=makeQuery(id+"F1.opExtrude","SWEPT_FACE",FACE,{"disambiguationData":[OSD([subQ0])]});var subQ5=makeQuery(id+"F5.opFillet","BLEND_FACE",FACE,{"disambiguationData":[OSD([subQ0,subQ2]),TDD([makeQuery(id+"F4.boolean.opBoolean","INTERSECT",EDGE,{"disambiguationData":[OD(0.0)],"derivedFrom":[subQ4,makeQuery(id+"F4.opExtrude","SWEPT_FACE",FACE,{"disambiguationData":[OSD([subQ2])]})]})])]});Q23=makeQuery(id+"FHcTJ38poMVbBsD_1.4.F5.opFillet","BLEND_EDGE",EDGE,{"blendedFrom":[makeQuery(id+"FHcTJ38poMVbBsD_1.4.F4.boolean.opBoolean","INTERSECT",EDGE,{"disambiguationData":[OD(0.0)],"derivedFrom":[makeQuery(id+"FHcTJ38poMVbBsD_1.3.F4.boolean.opBoolean","SPLIT",FACE,{"disambiguationData":[TD([subQ5])],"derivedFrom":makeQuery(id+"FHcTJ38poMVbBsD_1.2.F4.boolean.opBoolean","SPLIT",FACE,{"disambiguationData":[TD([subQ5])],"derivedFrom":makeQuery(id+"FHcTJ38poMVbBsD_1.1.F4.boolean.opBoolean","SPLIT",FACE,{"disambiguationData":[TD([subQ5])],"derivedFrom":subQ4})})}),makeQuery(id+"FHcTJ38poMVbBsD_1.4.F4.opExtrude","SWEPT_FACE",FACE,{"disambiguationData":[OSD([subQ2])]})]}),subQ1],"blendedInto":[subQ1]});}
            var Q24;
            {var subQ0=sQuery(id+"F0.wireOp",EDGE,"E0");var subQ1=makeQuery(id+"F1.opExtrude","CAP_FACE",FACE,{"disambiguationData":[OSD([subQ0])],"isStart":false});var subQ2=sQuery(id+"F3.wireOp",EDGE,"E5");var subQ4=makeQuery(id+"F1.opExtrude","SWEPT_FACE",FACE,{"disambiguationData":[OSD([subQ0])]});var subQ5=makeQuery(id+"F5.opFillet","BLEND_FACE",FACE,{"disambiguationData":[OSD([subQ0,subQ2]),TDD([makeQuery(id+"F4.boolean.opBoolean","INTERSECT",EDGE,{"disambiguationData":[OD(0.0)],"derivedFrom":[subQ4,makeQuery(id+"F4.opExtrude","SWEPT_FACE",FACE,{"disambiguationData":[OSD([subQ2])]})]})])]});Q24=makeQuery(id+"FHcTJ38poMVbBsD_1.4.F5.opFillet","BLEND_EDGE",EDGE,{"blendedFrom":[makeQuery(id+"FHcTJ38poMVbBsD_1.4.F4.boolean.opBoolean","INTERSECT",EDGE,{"disambiguationData":[OD(1.0)],"derivedFrom":[makeQuery(id+"FHcTJ38poMVbBsD_1.3.F4.boolean.opBoolean","SPLIT",FACE,{"disambiguationData":[TD([subQ5])],"derivedFrom":makeQuery(id+"FHcTJ38poMVbBsD_1.2.F4.boolean.opBoolean","SPLIT",FACE,{"disambiguationData":[TD([subQ5])],"derivedFrom":makeQuery(id+"FHcTJ38poMVbBsD_1.1.F4.boolean.opBoolean","SPLIT",FACE,{"disambiguationData":[TD([subQ5])],"derivedFrom":subQ4})})}),makeQuery(id+"FHcTJ38poMVbBsD_1.4.F4.opExtrude","SWEPT_FACE",FACE,{"disambiguationData":[OSD([subQ2])]})]}),subQ1],"blendedInto":[subQ1]});}
            var Q25;
            {var subQ0=sQuery(id+"F0.wireOp",EDGE,"E0");var subQ1=makeQuery(id+"F1.opExtrude","SWEPT_FACE",FACE,{"disambiguationData":[OSD([subQ0])]});var subQ3=sQuery(id+"F3.wireOp",EDGE,"E5");var subQ4=makeQuery(id+"FHcTJ38poMVbBsD_1.3.F4.opExtrude","SWEPT_FACE",FACE,{"disambiguationData":[OSD([subQ3])]});var subQ6=makeQuery(id+"F5.opFillet","BLEND_FACE",FACE,{"disambiguationData":[OSD([subQ0,subQ3]),TDD([makeQuery(id+"F4.boolean.opBoolean","INTERSECT",EDGE,{"disambiguationData":[OD(0.0)],"derivedFrom":[subQ1,makeQuery(id+"F4.opExtrude","SWEPT_FACE",FACE,{"disambiguationData":[OSD([subQ3])]})]})])]});Q25=makeQuery(id+"FHcTJ38poMVbBsD_1.4.F4.boolean.opBoolean","SPLIT",EDGE,{"disambiguationData":[TD([makeQuery(id+"FHcTJ38poMVbBsD_1.3.F5.opFillet","BLEND_FACE",FACE,{"disambiguationData":[OSD([subQ0,subQ3]),TDD([makeQuery(id+"FHcTJ38poMVbBsD_1.3.F4.boolean.opBoolean","INTERSECT",EDGE,{"disambiguationData":[OD(0.0)],"derivedFrom":[makeQuery(id+"FHcTJ38poMVbBsD_1.2.F4.boolean.opBoolean","SPLIT",FACE,{"disambiguationData":[TD([subQ6])],"derivedFrom":makeQuery(id+"FHcTJ38poMVbBsD_1.1.F4.boolean.opBoolean","SPLIT",FACE,{"disambiguationData":[TD([subQ6])],"derivedFrom":subQ1})}),subQ4]})])]})])],"derivedFrom":makeQuery(id+"FHcTJ38poMVbBsD_1.3.F4.boolean.opBoolean","SPLIT",EDGE,{"disambiguationData":[TD([subQ6])],"derivedFrom":makeQuery(id+"FHcTJ38poMVbBsD_1.2.F4.boolean.opBoolean","SPLIT",EDGE,{"disambiguationData":[TD([subQ6])],"derivedFrom":makeQuery(id+"FHcTJ38poMVbBsD_1.1.F4.boolean.opBoolean","SPLIT",EDGE,{"disambiguationData":[TD([subQ6])],"derivedFrom":makeQuery(id+"F1.opExtrude","CAP_EDGE",EDGE,{"disambiguationData":[OSD([subQ0])],"isStart":false})})})})});}
            var Q26;
            {var subQ0=sQuery(id+"F0.wireOp",EDGE,"E0");var subQ1=makeQuery(id+"F1.opExtrude","CAP_FACE",FACE,{"disambiguationData":[OSD([subQ0])],"isStart":false});var subQ2=sQuery(id+"F3.wireOp",EDGE,"E5");var subQ4=makeQuery(id+"F1.opExtrude","SWEPT_FACE",FACE,{"disambiguationData":[OSD([subQ0])]});var subQ5=makeQuery(id+"F5.opFillet","BLEND_FACE",FACE,{"disambiguationData":[OSD([subQ0,subQ2]),TDD([makeQuery(id+"F4.boolean.opBoolean","INTERSECT",EDGE,{"disambiguationData":[OD(0.0)],"derivedFrom":[subQ4,makeQuery(id+"F4.opExtrude","SWEPT_FACE",FACE,{"disambiguationData":[OSD([subQ2])]})]})])]});Q26=makeQuery(id+"FHcTJ38poMVbBsD_1.3.F5.opFillet","BLEND_EDGE",EDGE,{"blendedFrom":[makeQuery(id+"FHcTJ38poMVbBsD_1.3.F4.boolean.opBoolean","INTERSECT",EDGE,{"disambiguationData":[OD(0.0)],"derivedFrom":[makeQuery(id+"FHcTJ38poMVbBsD_1.2.F4.boolean.opBoolean","SPLIT",FACE,{"disambiguationData":[TD([subQ5])],"derivedFrom":makeQuery(id+"FHcTJ38poMVbBsD_1.1.F4.boolean.opBoolean","SPLIT",FACE,{"disambiguationData":[TD([subQ5])],"derivedFrom":subQ4})}),makeQuery(id+"FHcTJ38poMVbBsD_1.3.F4.opExtrude","SWEPT_FACE",FACE,{"disambiguationData":[OSD([subQ2])]})]}),subQ1],"blendedInto":[subQ1]});}
            var Q27;
            Q27=makeQuery(id+"FHcTJ38poMVbBsD_1.3.F4.boolean.opBoolean","INTERSECT",EDGE,{"derivedFrom":[makeQuery(id+"F1.opExtrude","CAP_FACE",FACE,{"disambiguationData":[OSD([sQuery(id+"F0.wireOp",EDGE,"E0")])],"isStart":false}),makeQuery(id+"FHcTJ38poMVbBsD_1.3.F4.opExtrude","SWEPT_FACE",FACE,{"disambiguationData":[OSD([sQuery(id+"F3.wireOp",EDGE,"E5")])]})]});
            var Q28;
            {var subQ0=sQuery(id+"F0.wireOp",EDGE,"E0");var subQ1=makeQuery(id+"F1.opExtrude","CAP_FACE",FACE,{"disambiguationData":[OSD([subQ0])],"isStart":false});var subQ2=sQuery(id+"F3.wireOp",EDGE,"E5");var subQ4=makeQuery(id+"F1.opExtrude","SWEPT_FACE",FACE,{"disambiguationData":[OSD([subQ0])]});var subQ5=makeQuery(id+"F5.opFillet","BLEND_FACE",FACE,{"disambiguationData":[OSD([subQ0,subQ2]),TDD([makeQuery(id+"F4.boolean.opBoolean","INTERSECT",EDGE,{"disambiguationData":[OD(0.0)],"derivedFrom":[subQ4,makeQuery(id+"F4.opExtrude","SWEPT_FACE",FACE,{"disambiguationData":[OSD([subQ2])]})]})])]});Q28=makeQuery(id+"FHcTJ38poMVbBsD_1.3.F5.opFillet","BLEND_EDGE",EDGE,{"blendedFrom":[makeQuery(id+"FHcTJ38poMVbBsD_1.3.F4.boolean.opBoolean","INTERSECT",EDGE,{"disambiguationData":[OD(1.0)],"derivedFrom":[makeQuery(id+"FHcTJ38poMVbBsD_1.2.F4.boolean.opBoolean","SPLIT",FACE,{"disambiguationData":[TD([subQ5])],"derivedFrom":makeQuery(id+"FHcTJ38poMVbBsD_1.1.F4.boolean.opBoolean","SPLIT",FACE,{"disambiguationData":[TD([subQ5])],"derivedFrom":subQ4})}),makeQuery(id+"FHcTJ38poMVbBsD_1.3.F4.opExtrude","SWEPT_FACE",FACE,{"disambiguationData":[OSD([subQ2])]})]}),subQ1],"blendedInto":[subQ1]});}
            var Q29;
            {var subQ0=sQuery(id+"F0.wireOp",EDGE,"E0");var subQ1=makeQuery(id+"F1.opExtrude","SWEPT_FACE",FACE,{"disambiguationData":[OSD([subQ0])]});var subQ3=sQuery(id+"F3.wireOp",EDGE,"E5");var subQ4=makeQuery(id+"FHcTJ38poMVbBsD_1.2.F4.opExtrude","SWEPT_FACE",FACE,{"disambiguationData":[OSD([subQ3])]});var subQ5=makeQuery(id+"F5.opFillet","BLEND_FACE",FACE,{"disambiguationData":[OSD([subQ0,subQ3]),TDD([makeQuery(id+"F4.boolean.opBoolean","INTERSECT",EDGE,{"disambiguationData":[OD(0.0)],"derivedFrom":[subQ1,makeQuery(id+"F4.opExtrude","SWEPT_FACE",FACE,{"disambiguationData":[OSD([subQ3])]})]})])]});Q29=makeQuery(id+"FHcTJ38poMVbBsD_1.3.F4.boolean.opBoolean","SPLIT",EDGE,{"disambiguationData":[TD([makeQuery(id+"FHcTJ38poMVbBsD_1.2.F5.opFillet","BLEND_FACE",FACE,{"disambiguationData":[OSD([subQ0,subQ3]),TDD([makeQuery(id+"FHcTJ38poMVbBsD_1.2.F4.boolean.opBoolean","INTERSECT",EDGE,{"disambiguationData":[OD(0.0)],"derivedFrom":[makeQuery(id+"FHcTJ38poMVbBsD_1.1.F4.boolean.opBoolean","SPLIT",FACE,{"disambiguationData":[TD([subQ5])],"derivedFrom":subQ1}),subQ4]})])]})])],"derivedFrom":makeQuery(id+"FHcTJ38poMVbBsD_1.2.F4.boolean.opBoolean","SPLIT",EDGE,{"disambiguationData":[TD([subQ5])],"derivedFrom":makeQuery(id+"FHcTJ38poMVbBsD_1.1.F4.boolean.opBoolean","SPLIT",EDGE,{"disambiguationData":[TD([subQ5])],"derivedFrom":makeQuery(id+"F1.opExtrude","CAP_EDGE",EDGE,{"disambiguationData":[OSD([subQ0])],"isStart":false})})})});}
            var Q30;
            {var subQ0=sQuery(id+"F0.wireOp",EDGE,"E0");var subQ1=makeQuery(id+"F1.opExtrude","CAP_FACE",FACE,{"disambiguationData":[OSD([subQ0])],"isStart":false});var subQ2=sQuery(id+"F3.wireOp",EDGE,"E5");var subQ3=makeQuery(id+"F1.opExtrude","SWEPT_FACE",FACE,{"disambiguationData":[OSD([subQ0])]});Q30=makeQuery(id+"FHcTJ38poMVbBsD_1.2.F5.opFillet","BLEND_EDGE",EDGE,{"blendedFrom":[makeQuery(id+"FHcTJ38poMVbBsD_1.2.F4.boolean.opBoolean","INTERSECT",EDGE,{"disambiguationData":[OD(0.0)],"derivedFrom":[makeQuery(id+"FHcTJ38poMVbBsD_1.1.F4.boolean.opBoolean","SPLIT",FACE,{"disambiguationData":[TD([makeQuery(id+"F5.opFillet","BLEND_FACE",FACE,{"disambiguationData":[OSD([subQ0,subQ2]),TDD([makeQuery(id+"F4.boolean.opBoolean","INTERSECT",EDGE,{"disambiguationData":[OD(0.0)],"derivedFrom":[subQ3,makeQuery(id+"F4.opExtrude","SWEPT_FACE",FACE,{"disambiguationData":[OSD([subQ2])]})]})])]})])],"derivedFrom":subQ3}),makeQuery(id+"FHcTJ38poMVbBsD_1.2.F4.opExtrude","SWEPT_FACE",FACE,{"disambiguationData":[OSD([subQ2])]})]}),subQ1],"blendedInto":[subQ1]});}
            var Q31;
            Q31=makeQuery(id+"FHcTJ38poMVbBsD_1.4.F4.boolean.opBoolean","INTERSECT",EDGE,{"derivedFrom":[makeQuery(id+"F1.opExtrude","CAP_FACE",FACE,{"disambiguationData":[OSD([sQuery(id+"F0.wireOp",EDGE,"E0")])],"isStart":false}),makeQuery(id+"FHcTJ38poMVbBsD_1.4.F4.opExtrude","SWEPT_FACE",FACE,{"disambiguationData":[OSD([sQuery(id+"F3.wireOp",EDGE,"E5")])]})]});
            fillet(context, id + "F11", {"entities" : qUnion([Q0, Q1, Q2, Q3, Q4, Q5, Q6, Q7, Q8, Q9, Q10, Q11, Q12, Q13, Q14, Q15, Q16, Q17, Q18, Q19, Q20, Q21, Q22, Q23, Q24, Q25, Q26, Q27, Q28, Q29, Q30, Q31]), "radius" : 2.45 * mm, "tangentPropagation" : true, "allowEdgeOverflow" : false});
        }
        {
            var Q0;
            Q0=makeQuery(id+"F10.opExtrude","CAP_FACE",FACE,{"disambiguationData":[OSD([sQuery(id+"F9.wireOp",EDGE,"E7")])],"isStart":false});
            var sketch = newSketch(context, id + "F12", { "sketchPlane" : qUnion([Q0])});
            skLineSegment(sketch, "E8.bottom", {"start": v(-3.46, 1.6) * mm, "end": v(3.46, 1.6) * mm});
            skLineSegment(sketch, "E8.top", {"start": v(-3.46, -1.6) * mm, "end": v(3.46, -1.6) * mm});
            skLineSegment(sketch, "E8.left", {"start": v(-3.46, 1.6) * mm, "end": v(-3.46, -1.6) * mm});
            skLineSegment(sketch, "E8.right", {"start": v(3.46, 1.6) * mm, "end": v(3.46, -1.6) * mm});
            skPoint(sketch, "E8.middle", {"position": v(0, 0) * mm});
            skSolve(sketch);
        }
        {
            var Q0;
            {var subQ0=sQuery(id+"F12.wireOp",EDGE,"E8.top");Q0=makeQuery(id+"F12.imprint","IMPRINT",FACE,{"disambiguationData":[TD([[makeQuery(id+"F12.imprint","IMPRINT",EDGE,{"derivedFrom":subQ0}),-1.0]])]});}
            var sketch = newSketch(context, id + "F13", { "sketchPlane" : qUnion([Q0])});
            skLineSegment(sketch, "E9.bottom", {"start": v(1.6, 3.46) * mm, "end": v(-1.6, 3.46) * mm});
            skLineSegment(sketch, "E9.top", {"start": v(1.6, -3.46) * mm, "end": v(-1.6, -3.46) * mm});
            skLineSegment(sketch, "E9.left", {"start": v(1.6, 3.46) * mm, "end": v(1.6, -3.46) * mm});
            skLineSegment(sketch, "E9.right", {"start": v(-1.6, 3.46) * mm, "end": v(-1.6, -3.46) * mm});
            skPoint(sketch, "E9.middle", {"position": v(0, 0) * mm});
            skSolve(sketch);
        }
        {
            var Q0;
            Q0=makeQuery(id+"F12.imprint","IMPRINT",FACE,{"disambiguationData":[TD([[makeQuery(id+"F12.imprint","IMPRINT",EDGE,{"derivedFrom":sQuery(id+"F12.wireOp",EDGE,"E8.bottom")}),-1.0]])]});
            extrude(context, id + "F14", {"entities" : qUnion([Q0]), "operationType" : NewBodyOperationType.ADD, "depth" : 12.7 * mm});
        }
        {
            var Q0;
            {var subQ0=sQuery(id+"F13.wireOp",EDGE,"E9.bottom");Q0=makeQuery(id+"F13.imprint","IMPRINT",FACE,{"disambiguationData":[TD([[makeQuery(id+"F13.imprint","IMPRINT",EDGE,{"derivedFrom":subQ0}),1.0]])]});}
            var Q1;
            {var subQ0=sQuery(id+"F13.wireOp",EDGE,"E9.top");Q1=makeQuery(id+"F13.imprint","IMPRINT",FACE,{"disambiguationData":[TD([[makeQuery(id+"F13.imprint","IMPRINT",EDGE,{"derivedFrom":subQ0}),-1.0]])]});}
            extrude(context, id + "F15", {"entities" : qUnion([Q0, Q1]), "operationType" : NewBodyOperationType.ADD, "depth" : 12.7 * mm});
        }
        {
            var Q0;
            {var subQ1=sQuery(id+"F12.wireOp",EDGE,"E8.left");var subQ2=sQuery(id+"F12.wireOp",EDGE,"E8.bottom");Q0=makeQuery(id+"F15.boolean.opBoolean","SPLIT",EDGE,{"disambiguationData":[TD([makeQuery(id+"F14.opExtrude","SWEPT_FACE",FACE,{"disambiguationData":[OSD([subQ1])]})])],"derivedFrom":makeQuery(id+"F14.opExtrude","CAP_EDGE",EDGE,{"disambiguationData":[OSD([subQ2])],"isStart":false})});}
            var Q1;
            {var subQ0=sQuery(id+"F13.wireOp",EDGE,"E9.right");var subQ2=sQuery(id+"F12.wireOp",EDGE,"E8.bottom");Q1=makeQuery(id+"F15.boolean.opBoolean","SPLIT",EDGE,{"disambiguationData":[TD([makeQuery(id+"F14.opExtrude","SWEPT_FACE",FACE,{"disambiguationData":[OSD([subQ2])]})])],"derivedFrom":makeQuery(id+"F15.opExtrude","CAP_EDGE",EDGE,{"disambiguationData":[OSD([subQ0])],"isStart":false})});}
            var Q2;
            {var subQ1=sQuery(id+"F12.wireOp",EDGE,"E8.right");var subQ2=sQuery(id+"F12.wireOp",EDGE,"E8.bottom");Q2=makeQuery(id+"F15.boolean.opBoolean","SPLIT",EDGE,{"disambiguationData":[TD([makeQuery(id+"F14.opExtrude","SWEPT_FACE",FACE,{"disambiguationData":[OSD([subQ1])]})])],"derivedFrom":makeQuery(id+"F14.opExtrude","CAP_EDGE",EDGE,{"disambiguationData":[OSD([subQ2])],"isStart":false})});}
            var Q3;
            {var subQ0=sQuery(id+"F13.wireOp",EDGE,"E9.left");var subQ2=sQuery(id+"F12.wireOp",EDGE,"E8.bottom");Q3=makeQuery(id+"F15.boolean.opBoolean","SPLIT",EDGE,{"disambiguationData":[TD([makeQuery(id+"F14.opExtrude","SWEPT_FACE",FACE,{"disambiguationData":[OSD([subQ2])]})])],"derivedFrom":makeQuery(id+"F15.opExtrude","CAP_EDGE",EDGE,{"disambiguationData":[OSD([subQ0])],"isStart":false})});}
            var Q4;
            {var subQ1=sQuery(id+"F12.wireOp",EDGE,"E8.right");var subQ2=sQuery(id+"F12.wireOp",EDGE,"E8.top");Q4=makeQuery(id+"F15.boolean.opBoolean","SPLIT",EDGE,{"disambiguationData":[TD([makeQuery(id+"F14.opExtrude","SWEPT_FACE",FACE,{"disambiguationData":[OSD([subQ1])]})])],"derivedFrom":makeQuery(id+"F14.opExtrude","CAP_EDGE",EDGE,{"disambiguationData":[OSD([subQ2])],"isStart":false})});}
            var Q5;
            {var subQ1=sQuery(id+"F13.wireOp",EDGE,"E9.left");var subQ2=sQuery(id+"F12.wireOp",EDGE,"E8.top");Q5=makeQuery(id+"F15.boolean.opBoolean","SPLIT",EDGE,{"disambiguationData":[TD([makeQuery(id+"F14.opExtrude","SWEPT_FACE",FACE,{"disambiguationData":[OSD([subQ2])]})])],"derivedFrom":makeQuery(id+"F15.opExtrude","CAP_EDGE",EDGE,{"disambiguationData":[OSD([subQ1])],"isStart":false})});}
            var Q6;
            {var subQ1=sQuery(id+"F12.wireOp",EDGE,"E8.left");var subQ2=sQuery(id+"F12.wireOp",EDGE,"E8.top");Q6=makeQuery(id+"F15.boolean.opBoolean","SPLIT",EDGE,{"disambiguationData":[TD([makeQuery(id+"F14.opExtrude","SWEPT_FACE",FACE,{"disambiguationData":[OSD([subQ1])]})])],"derivedFrom":makeQuery(id+"F14.opExtrude","CAP_EDGE",EDGE,{"disambiguationData":[OSD([subQ2])],"isStart":false})});}
            var Q7;
            {var subQ1=sQuery(id+"F13.wireOp",EDGE,"E9.right");var subQ2=sQuery(id+"F12.wireOp",EDGE,"E8.top");Q7=makeQuery(id+"F15.boolean.opBoolean","SPLIT",EDGE,{"disambiguationData":[TD([makeQuery(id+"F14.opExtrude","SWEPT_FACE",FACE,{"disambiguationData":[OSD([subQ2])]})])],"derivedFrom":makeQuery(id+"F15.opExtrude","CAP_EDGE",EDGE,{"disambiguationData":[OSD([subQ1])],"isStart":false})});}
            chamfer(context, id + "F16", {"entities" : qUnion([Q0, Q1, Q2, Q3, Q4, Q5, Q6, Q7]), "width" : 5.08 * mm, "tangentPropagation" : true});
        }
        {
            var Q0;
            {var subQ0=sQuery(id+"F12.wireOp",EDGE,"E8.right");var subQ1=makeQuery(id+"F14.opExtrude","SWEPT_FACE",FACE,{"disambiguationData":[OSD([subQ0])]});var subQ2=sQuery(id+"F12.wireOp",EDGE,"E8.bottom");var subQ8=makeQuery(id+"F14.opExtrude","SWEPT_FACE",FACE,{"disambiguationData":[OSD([subQ2])]});Q0=makeQuery(id+"F16.opChamfer","BLEND_EDGE",EDGE,{"blendedFrom":[makeQuery(id+"F15.boolean.opBoolean","SPLIT",EDGE,{"disambiguationData":[TD([subQ1])],"derivedFrom":makeQuery(id+"F14.opExtrude","CAP_EDGE",EDGE,{"disambiguationData":[OSD([subQ2])],"isStart":false})}),makeQuery(id+"F15.boolean.opBoolean","SPLIT",FACE,{"disambiguationData":[TD([subQ1])],"derivedFrom":subQ8})],"blendedInto":[makeQuery(id+"F15.boolean.opBoolean","SPLIT",FACE,{"disambiguationData":[TD([subQ1])],"derivedFrom":subQ8})]});}
            var Q1;
            {var subQ2=sQuery(id+"F12.wireOp",EDGE,"E8.bottom");var subQ4=makeQuery(id+"F14.opExtrude","SWEPT_FACE",FACE,{"disambiguationData":[OSD([subQ2])]});var subQ5=sQuery(id+"F13.wireOp",EDGE,"E9.left");var subQ7=makeQuery(id+"F15.opExtrude","SWEPT_FACE",FACE,{"disambiguationData":[OSD([subQ5])]});Q1=makeQuery(id+"F16.opChamfer","BLEND_EDGE",EDGE,{"blendedFrom":[makeQuery(id+"F15.boolean.opBoolean","SPLIT",EDGE,{"disambiguationData":[TD([subQ4])],"derivedFrom":makeQuery(id+"F15.opExtrude","CAP_EDGE",EDGE,{"disambiguationData":[OSD([subQ5])],"isStart":false})}),makeQuery(id+"F15.boolean.opBoolean","SPLIT",FACE,{"disambiguationData":[TD([subQ4])],"derivedFrom":subQ7})],"blendedInto":[makeQuery(id+"F15.boolean.opBoolean","SPLIT",FACE,{"disambiguationData":[TD([subQ4])],"derivedFrom":subQ7})]});}
            var Q2;
            {var subQ0=sQuery(id+"F12.wireOp",EDGE,"E8.left");var subQ1=makeQuery(id+"F14.opExtrude","SWEPT_FACE",FACE,{"disambiguationData":[OSD([subQ0])]});var subQ4=sQuery(id+"F12.wireOp",EDGE,"E8.top");var subQ8=makeQuery(id+"F14.opExtrude","SWEPT_FACE",FACE,{"disambiguationData":[OSD([subQ4])]});Q2=makeQuery(id+"F16.opChamfer","BLEND_EDGE",EDGE,{"blendedFrom":[makeQuery(id+"F15.boolean.opBoolean","SPLIT",EDGE,{"disambiguationData":[TD([subQ1])],"derivedFrom":makeQuery(id+"F14.opExtrude","CAP_EDGE",EDGE,{"disambiguationData":[OSD([subQ4])],"isStart":false})}),makeQuery(id+"F15.boolean.opBoolean","SPLIT",FACE,{"disambiguationData":[TD([subQ1])],"derivedFrom":subQ8})],"blendedInto":[makeQuery(id+"F15.boolean.opBoolean","SPLIT",FACE,{"disambiguationData":[TD([subQ1])],"derivedFrom":subQ8})]});}
            var Q3;
            {var subQ0=sQuery(id+"F13.wireOp",EDGE,"E9.right");var subQ3=sQuery(id+"F12.wireOp",EDGE,"E8.top");var subQ4=makeQuery(id+"F14.opExtrude","SWEPT_FACE",FACE,{"disambiguationData":[OSD([subQ3])]});var subQ7=makeQuery(id+"F15.opExtrude","SWEPT_FACE",FACE,{"disambiguationData":[OSD([subQ0])]});Q3=makeQuery(id+"F16.opChamfer","BLEND_EDGE",EDGE,{"blendedFrom":[makeQuery(id+"F15.boolean.opBoolean","SPLIT",EDGE,{"disambiguationData":[TD([subQ4])],"derivedFrom":makeQuery(id+"F15.opExtrude","CAP_EDGE",EDGE,{"disambiguationData":[OSD([subQ0])],"isStart":false})}),makeQuery(id+"F15.boolean.opBoolean","SPLIT",FACE,{"disambiguationData":[TD([subQ4])],"derivedFrom":subQ7})],"blendedInto":[makeQuery(id+"F15.boolean.opBoolean","SPLIT",FACE,{"disambiguationData":[TD([subQ4])],"derivedFrom":subQ7})]});}
            var Q4;
            {var subQ0=sQuery(id+"F13.wireOp",EDGE,"E9.left");var subQ3=sQuery(id+"F12.wireOp",EDGE,"E8.top");var subQ4=makeQuery(id+"F14.opExtrude","SWEPT_FACE",FACE,{"disambiguationData":[OSD([subQ3])]});var subQ7=makeQuery(id+"F15.opExtrude","SWEPT_FACE",FACE,{"disambiguationData":[OSD([subQ0])]});Q4=makeQuery(id+"F16.opChamfer","BLEND_EDGE",EDGE,{"blendedFrom":[makeQuery(id+"F15.boolean.opBoolean","SPLIT",EDGE,{"disambiguationData":[TD([subQ4])],"derivedFrom":makeQuery(id+"F15.opExtrude","CAP_EDGE",EDGE,{"disambiguationData":[OSD([subQ0])],"isStart":false})}),makeQuery(id+"F15.boolean.opBoolean","SPLIT",FACE,{"disambiguationData":[TD([subQ4])],"derivedFrom":subQ7})],"blendedInto":[makeQuery(id+"F15.boolean.opBoolean","SPLIT",FACE,{"disambiguationData":[TD([subQ4])],"derivedFrom":subQ7})]});}
            var Q5;
            {var subQ0=sQuery(id+"F12.wireOp",EDGE,"E8.right");var subQ1=makeQuery(id+"F14.opExtrude","SWEPT_FACE",FACE,{"disambiguationData":[OSD([subQ0])]});var subQ2=sQuery(id+"F12.wireOp",EDGE,"E8.top");var subQ8=makeQuery(id+"F14.opExtrude","SWEPT_FACE",FACE,{"disambiguationData":[OSD([subQ2])]});Q5=makeQuery(id+"F16.opChamfer","BLEND_EDGE",EDGE,{"blendedFrom":[makeQuery(id+"F15.boolean.opBoolean","SPLIT",EDGE,{"disambiguationData":[TD([subQ1])],"derivedFrom":makeQuery(id+"F14.opExtrude","CAP_EDGE",EDGE,{"disambiguationData":[OSD([subQ2])],"isStart":false})}),makeQuery(id+"F15.boolean.opBoolean","SPLIT",FACE,{"disambiguationData":[TD([subQ1])],"derivedFrom":subQ8})],"blendedInto":[makeQuery(id+"F15.boolean.opBoolean","SPLIT",FACE,{"disambiguationData":[TD([subQ1])],"derivedFrom":subQ8})]});}
            var Q6;
            {var subQ0=sQuery(id+"F12.wireOp",EDGE,"E8.left");var subQ1=makeQuery(id+"F14.opExtrude","SWEPT_FACE",FACE,{"disambiguationData":[OSD([subQ0])]});var subQ4=sQuery(id+"F12.wireOp",EDGE,"E8.bottom");var subQ8=makeQuery(id+"F14.opExtrude","SWEPT_FACE",FACE,{"disambiguationData":[OSD([subQ4])]});Q6=makeQuery(id+"F16.opChamfer","BLEND_EDGE",EDGE,{"blendedFrom":[makeQuery(id+"F15.boolean.opBoolean","SPLIT",EDGE,{"disambiguationData":[TD([subQ1])],"derivedFrom":makeQuery(id+"F14.opExtrude","CAP_EDGE",EDGE,{"disambiguationData":[OSD([subQ4])],"isStart":false})}),makeQuery(id+"F15.boolean.opBoolean","SPLIT",FACE,{"disambiguationData":[TD([subQ1])],"derivedFrom":subQ8})],"blendedInto":[makeQuery(id+"F15.boolean.opBoolean","SPLIT",FACE,{"disambiguationData":[TD([subQ1])],"derivedFrom":subQ8})]});}
            var Q7;
            {var subQ2=sQuery(id+"F12.wireOp",EDGE,"E8.bottom");var subQ4=makeQuery(id+"F14.opExtrude","SWEPT_FACE",FACE,{"disambiguationData":[OSD([subQ2])]});var subQ5=sQuery(id+"F13.wireOp",EDGE,"E9.right");var subQ7=makeQuery(id+"F15.opExtrude","SWEPT_FACE",FACE,{"disambiguationData":[OSD([subQ5])]});Q7=makeQuery(id+"F16.opChamfer","BLEND_EDGE",EDGE,{"blendedFrom":[makeQuery(id+"F15.boolean.opBoolean","SPLIT",EDGE,{"disambiguationData":[TD([subQ4])],"derivedFrom":makeQuery(id+"F15.opExtrude","CAP_EDGE",EDGE,{"disambiguationData":[OSD([subQ5])],"isStart":false})}),makeQuery(id+"F15.boolean.opBoolean","SPLIT",FACE,{"disambiguationData":[TD([subQ4])],"derivedFrom":subQ7})],"blendedInto":[makeQuery(id+"F15.boolean.opBoolean","SPLIT",FACE,{"disambiguationData":[TD([subQ4])],"derivedFrom":subQ7})]});}
            chamfer(context, id + "F17", {"entities" : qUnion([Q0, Q1, Q2, Q3, Q4, Q5, Q6, Q7]), "width" : 2.16 * mm, "tangentPropagation" : true});
        }
        {
            var Q0;
            Q0=makeQuery(id+"F15.boolean.opBoolean","INTERSECT",EDGE,{"derivedFrom":[makeQuery(id+"F14.opExtrude","SWEPT_FACE",FACE,{"disambiguationData":[OSD([sQuery(id+"F12.wireOp",EDGE,"E8.bottom")])]}),makeQuery(id+"F15.opExtrude","SWEPT_FACE",FACE,{"disambiguationData":[OSD([sQuery(id+"F13.wireOp",EDGE,"E9.right")])]})]});
            var Q1;
            {var subQ2=sQuery(id+"F12.wireOp",EDGE,"E8.left");var subQ3=sQuery(id+"F12.wireOp",EDGE,"E8.bottom");var subQ5=makeQuery(id+"F14.opExtrude","SWEPT_FACE",FACE,{"disambiguationData":[OSD([subQ3])]});var subQ8=sQuery(id+"F13.wireOp",EDGE,"E9.right");var subQ10=makeQuery(id+"F15.opExtrude","SWEPT_FACE",FACE,{"disambiguationData":[OSD([subQ8])]});var subQ11=makeQuery(id+"F14.opExtrude","SWEPT_FACE",FACE,{"disambiguationData":[OSD([subQ2])]});Q1=makeQuery(id+"F17.opChamfer","BLEND_EDGE",EDGE,{"blendedFrom":[makeQuery(id+"F16.opChamfer","BLEND_EDGE",EDGE,{"blendedFrom":[makeQuery(id+"F15.boolean.opBoolean","SPLIT",EDGE,{"disambiguationData":[TD([subQ11])],"derivedFrom":makeQuery(id+"F14.opExtrude","CAP_EDGE",EDGE,{"disambiguationData":[OSD([subQ3])],"isStart":false})}),makeQuery(id+"F15.boolean.opBoolean","SPLIT",FACE,{"disambiguationData":[TD([subQ11])],"derivedFrom":subQ5})],"blendedInto":[makeQuery(id+"F15.boolean.opBoolean","SPLIT",FACE,{"disambiguationData":[TD([subQ11])],"derivedFrom":subQ5})]}),makeQuery(id+"F16.opChamfer","BLEND_EDGE",EDGE,{"blendedFrom":[makeQuery(id+"F15.boolean.opBoolean","SPLIT",EDGE,{"disambiguationData":[TD([subQ5])],"derivedFrom":makeQuery(id+"F15.opExtrude","CAP_EDGE",EDGE,{"disambiguationData":[OSD([subQ8])],"isStart":false})}),makeQuery(id+"F15.boolean.opBoolean","SPLIT",FACE,{"disambiguationData":[TD([subQ5])],"derivedFrom":subQ10})],"blendedInto":[makeQuery(id+"F15.boolean.opBoolean","SPLIT",FACE,{"disambiguationData":[TD([subQ5])],"derivedFrom":subQ10})]})],"blendedInto":[]});}
            var Q2;
            Q2=makeQuery(id+"F15.boolean.opBoolean","INTERSECT",EDGE,{"derivedFrom":[makeQuery(id+"F14.opExtrude","SWEPT_FACE",FACE,{"disambiguationData":[OSD([sQuery(id+"F12.wireOp",EDGE,"E8.top")])]}),makeQuery(id+"F15.opExtrude","SWEPT_FACE",FACE,{"disambiguationData":[OSD([sQuery(id+"F13.wireOp",EDGE,"E9.right")])]})]});
            var Q3;
            {var subQ0=sQuery(id+"F13.wireOp",EDGE,"E9.right");var subQ3=sQuery(id+"F12.wireOp",EDGE,"E8.top");var subQ4=makeQuery(id+"F14.opExtrude","SWEPT_FACE",FACE,{"disambiguationData":[OSD([subQ3])]});var subQ7=sQuery(id+"F12.wireOp",EDGE,"E8.left");var subQ10=makeQuery(id+"F15.opExtrude","SWEPT_FACE",FACE,{"disambiguationData":[OSD([subQ0])]});var subQ11=makeQuery(id+"F14.opExtrude","SWEPT_FACE",FACE,{"disambiguationData":[OSD([subQ7])]});Q3=makeQuery(id+"F17.opChamfer","BLEND_EDGE",EDGE,{"blendedFrom":[makeQuery(id+"F16.opChamfer","BLEND_EDGE",EDGE,{"blendedFrom":[makeQuery(id+"F15.boolean.opBoolean","SPLIT",EDGE,{"disambiguationData":[TD([subQ11])],"derivedFrom":makeQuery(id+"F14.opExtrude","CAP_EDGE",EDGE,{"disambiguationData":[OSD([subQ3])],"isStart":false})}),makeQuery(id+"F15.boolean.opBoolean","SPLIT",FACE,{"disambiguationData":[TD([subQ11])],"derivedFrom":subQ4})],"blendedInto":[makeQuery(id+"F15.boolean.opBoolean","SPLIT",FACE,{"disambiguationData":[TD([subQ11])],"derivedFrom":subQ4})]}),makeQuery(id+"F16.opChamfer","BLEND_EDGE",EDGE,{"blendedFrom":[makeQuery(id+"F15.boolean.opBoolean","SPLIT",EDGE,{"disambiguationData":[TD([subQ4])],"derivedFrom":makeQuery(id+"F15.opExtrude","CAP_EDGE",EDGE,{"disambiguationData":[OSD([subQ0])],"isStart":false})}),makeQuery(id+"F15.boolean.opBoolean","SPLIT",FACE,{"disambiguationData":[TD([subQ4])],"derivedFrom":subQ10})],"blendedInto":[makeQuery(id+"F15.boolean.opBoolean","SPLIT",FACE,{"disambiguationData":[TD([subQ4])],"derivedFrom":subQ10})]})],"blendedInto":[]});}
            var Q4;
            {var subQ2=sQuery(id+"F12.wireOp",EDGE,"E8.right");var subQ3=sQuery(id+"F12.wireOp",EDGE,"E8.bottom");var subQ5=makeQuery(id+"F14.opExtrude","SWEPT_FACE",FACE,{"disambiguationData":[OSD([subQ3])]});var subQ8=sQuery(id+"F13.wireOp",EDGE,"E9.left");var subQ10=makeQuery(id+"F15.opExtrude","SWEPT_FACE",FACE,{"disambiguationData":[OSD([subQ8])]});var subQ11=makeQuery(id+"F14.opExtrude","SWEPT_FACE",FACE,{"disambiguationData":[OSD([subQ2])]});Q4=makeQuery(id+"F17.opChamfer","BLEND_EDGE",EDGE,{"blendedFrom":[makeQuery(id+"F16.opChamfer","BLEND_EDGE",EDGE,{"blendedFrom":[makeQuery(id+"F15.boolean.opBoolean","SPLIT",EDGE,{"disambiguationData":[TD([subQ11])],"derivedFrom":makeQuery(id+"F14.opExtrude","CAP_EDGE",EDGE,{"disambiguationData":[OSD([subQ3])],"isStart":false})}),makeQuery(id+"F15.boolean.opBoolean","SPLIT",FACE,{"disambiguationData":[TD([subQ11])],"derivedFrom":subQ5})],"blendedInto":[makeQuery(id+"F15.boolean.opBoolean","SPLIT",FACE,{"disambiguationData":[TD([subQ11])],"derivedFrom":subQ5})]}),makeQuery(id+"F16.opChamfer","BLEND_EDGE",EDGE,{"blendedFrom":[makeQuery(id+"F15.boolean.opBoolean","SPLIT",EDGE,{"disambiguationData":[TD([subQ5])],"derivedFrom":makeQuery(id+"F15.opExtrude","CAP_EDGE",EDGE,{"disambiguationData":[OSD([subQ8])],"isStart":false})}),makeQuery(id+"F15.boolean.opBoolean","SPLIT",FACE,{"disambiguationData":[TD([subQ5])],"derivedFrom":subQ10})],"blendedInto":[makeQuery(id+"F15.boolean.opBoolean","SPLIT",FACE,{"disambiguationData":[TD([subQ5])],"derivedFrom":subQ10})]})],"blendedInto":[]});}
            var Q5;
            {var subQ0=sQuery(id+"F13.wireOp",EDGE,"E9.left");var subQ3=sQuery(id+"F12.wireOp",EDGE,"E8.top");var subQ4=makeQuery(id+"F14.opExtrude","SWEPT_FACE",FACE,{"disambiguationData":[OSD([subQ3])]});var subQ7=sQuery(id+"F12.wireOp",EDGE,"E8.right");var subQ10=makeQuery(id+"F15.opExtrude","SWEPT_FACE",FACE,{"disambiguationData":[OSD([subQ0])]});var subQ11=makeQuery(id+"F14.opExtrude","SWEPT_FACE",FACE,{"disambiguationData":[OSD([subQ7])]});Q5=makeQuery(id+"F17.opChamfer","BLEND_EDGE",EDGE,{"blendedFrom":[makeQuery(id+"F16.opChamfer","BLEND_EDGE",EDGE,{"blendedFrom":[makeQuery(id+"F15.boolean.opBoolean","SPLIT",EDGE,{"disambiguationData":[TD([subQ11])],"derivedFrom":makeQuery(id+"F14.opExtrude","CAP_EDGE",EDGE,{"disambiguationData":[OSD([subQ3])],"isStart":false})}),makeQuery(id+"F15.boolean.opBoolean","SPLIT",FACE,{"disambiguationData":[TD([subQ11])],"derivedFrom":subQ4})],"blendedInto":[makeQuery(id+"F15.boolean.opBoolean","SPLIT",FACE,{"disambiguationData":[TD([subQ11])],"derivedFrom":subQ4})]}),makeQuery(id+"F16.opChamfer","BLEND_EDGE",EDGE,{"blendedFrom":[makeQuery(id+"F15.boolean.opBoolean","SPLIT",EDGE,{"disambiguationData":[TD([subQ4])],"derivedFrom":makeQuery(id+"F15.opExtrude","CAP_EDGE",EDGE,{"disambiguationData":[OSD([subQ0])],"isStart":false})}),makeQuery(id+"F15.boolean.opBoolean","SPLIT",FACE,{"disambiguationData":[TD([subQ4])],"derivedFrom":subQ10})],"blendedInto":[makeQuery(id+"F15.boolean.opBoolean","SPLIT",FACE,{"disambiguationData":[TD([subQ4])],"derivedFrom":subQ10})]})],"blendedInto":[]});}
            var Q6;
            Q6=makeQuery(id+"F15.boolean.opBoolean","INTERSECT",EDGE,{"derivedFrom":[makeQuery(id+"F14.opExtrude","SWEPT_FACE",FACE,{"disambiguationData":[OSD([sQuery(id+"F12.wireOp",EDGE,"E8.top")])]}),makeQuery(id+"F15.opExtrude","SWEPT_FACE",FACE,{"disambiguationData":[OSD([sQuery(id+"F13.wireOp",EDGE,"E9.left")])]})]});
            var Q7;
            Q7=makeQuery(id+"F15.boolean.opBoolean","INTERSECT",EDGE,{"derivedFrom":[makeQuery(id+"F14.opExtrude","SWEPT_FACE",FACE,{"disambiguationData":[OSD([sQuery(id+"F12.wireOp",EDGE,"E8.bottom")])]}),makeQuery(id+"F15.opExtrude","SWEPT_FACE",FACE,{"disambiguationData":[OSD([sQuery(id+"F13.wireOp",EDGE,"E9.left")])]})]});
            fillet(context, id + "F18", {"entities" : qUnion([Q0, Q1, Q2, Q3, Q4, Q5, Q6, Q7]), "radius" : 0.76 * mm, "tangentPropagation" : true, "allowEdgeOverflow" : false});
        }
    });
